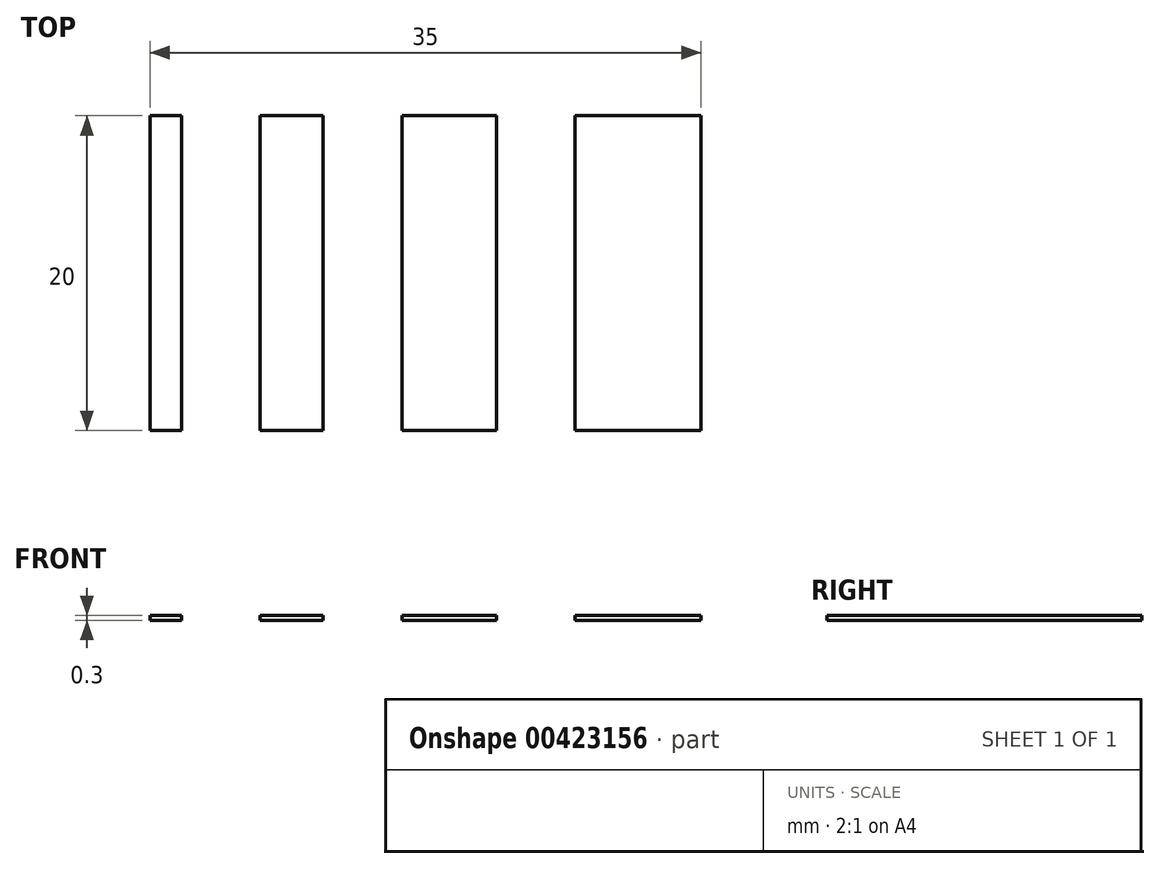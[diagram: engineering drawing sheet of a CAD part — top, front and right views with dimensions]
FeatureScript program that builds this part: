
annotation { "Feature Type Name" : "Feature", "Feature Type Description" : "" }
export const myFeature = defineFeature(function(context is Context, id is Id, definition is map)
    precondition{}
    {
        {
            var Q0;
            Q0=qCreatedBy(makeId("Top.planeOp"),FACE);
            var sketch = newSketch(context, id + "F0", { "sketchPlane" : qUnion([Q0])});
            skLineSegment(sketch, "E0.bottom", {"start": v(-14.06, 10) * mm, "end": v(-16.06, 10) * mm});
            skLineSegment(sketch, "E0.top", {"start": v(-14.06, -10) * mm, "end": v(-16.06, -10) * mm});
            skLineSegment(sketch, "E0.left", {"start": v(-14.06, 10) * mm, "end": v(-14.06, -10) * mm});
            skLineSegment(sketch, "E0.right", {"start": v(-16.06, 10) * mm, "end": v(-16.06, -10) * mm});
            skPoint(sketch, "E0.middle", {"position": v(-15.06, 0) * mm});
            skLineSegment(sketch, "E1.bottom", {"start": v(-5.06, 10) * mm, "end": v(-9.06, 10) * mm});
            skLineSegment(sketch, "E1.top", {"start": v(-5.06, -10) * mm, "end": v(-9.06, -10) * mm});
            skLineSegment(sketch, "E1.left", {"start": v(-5.06, 10) * mm, "end": v(-5.06, -10) * mm});
            skLineSegment(sketch, "E1.right", {"start": v(-9.06, 10) * mm, "end": v(-9.06, -10) * mm});
            skPoint(sketch, "E1.middle", {"position": v(-7.06, 0) * mm});
            skLineSegment(sketch, "E2.bottom", {"start": v(5.94, 10) * mm, "end": v(-0.06, 10) * mm});
            skLineSegment(sketch, "E2.top", {"start": v(5.94, -10) * mm, "end": v(-0.06, -10) * mm});
            skLineSegment(sketch, "E2.left", {"start": v(5.94, 10) * mm, "end": v(5.94, -10) * mm});
            skLineSegment(sketch, "E2.right", {"start": v(-0.06, 10) * mm, "end": v(-0.06, -10) * mm});
            skPoint(sketch, "E2.middle", {"position": v(2.94, 0) * mm});
            skLineSegment(sketch, "E3.bottom", {"start": v(18.94, 10) * mm, "end": v(10.94, 10) * mm});
            skLineSegment(sketch, "E3.top", {"start": v(18.94, -10) * mm, "end": v(10.94, -10) * mm});
            skLineSegment(sketch, "E3.left", {"start": v(18.94, 10) * mm, "end": v(18.94, -10) * mm});
            skLineSegment(sketch, "E3.right", {"start": v(10.94, 10) * mm, "end": v(10.94, -10) * mm});
            skPoint(sketch, "E3.middle", {"position": v(14.94, 0) * mm});
            skSolve(sketch);
        }
        {
            var Q0;
            Q0 = qSketchRegion(id + "F0", true);
            extrude(context, id + "F1", {"entities" : qUnion([Q0]), "depth" : 0.3 * mm, "offsetDistance" : 25 * mm});
        }
    });
